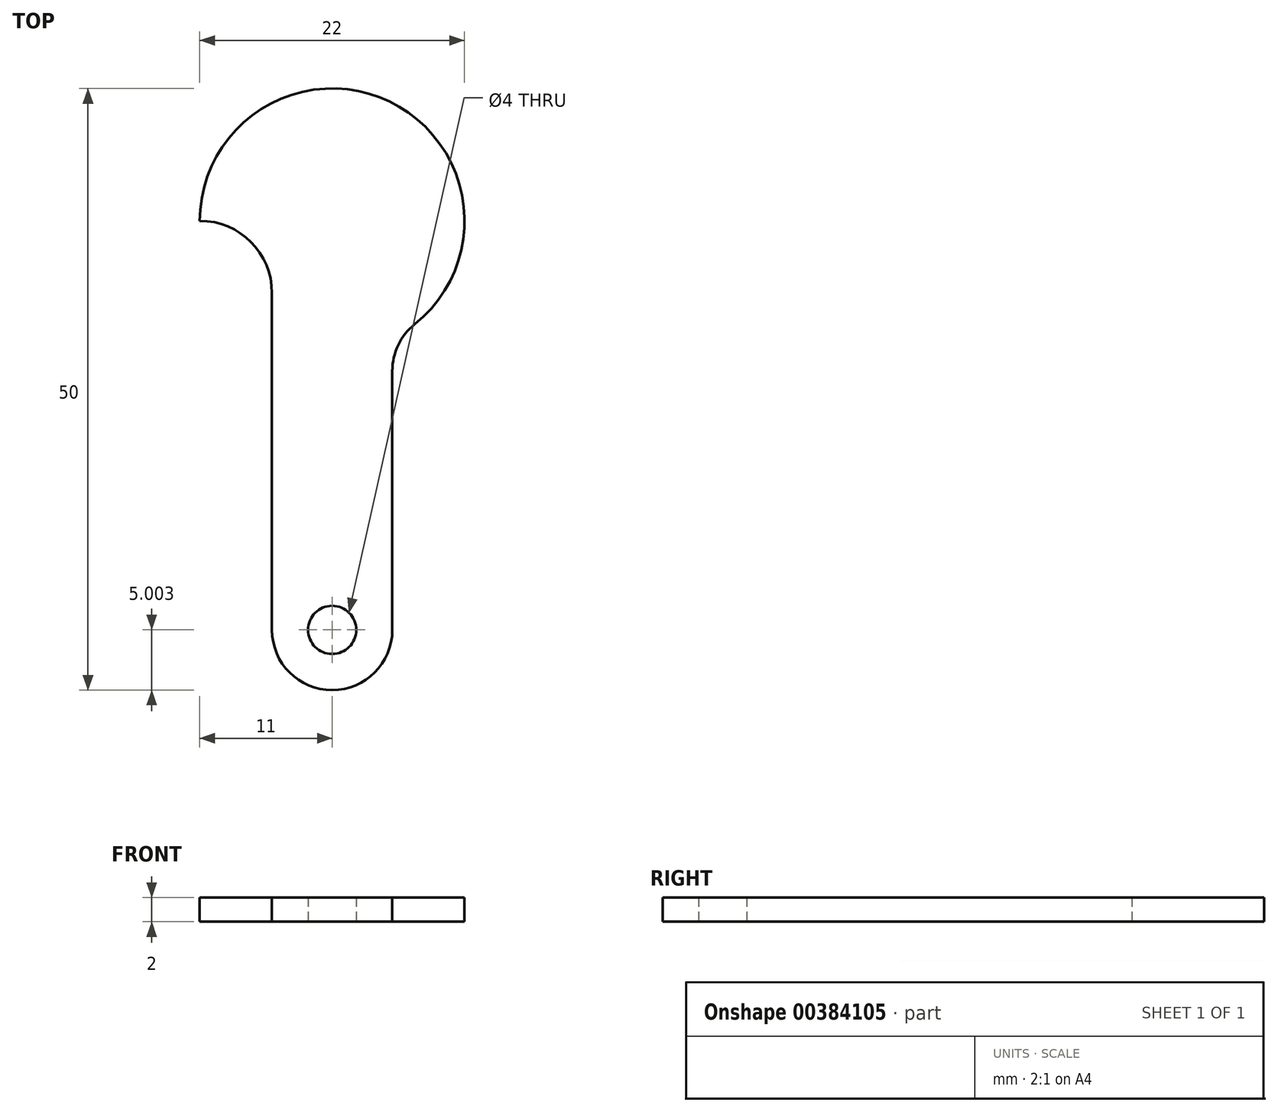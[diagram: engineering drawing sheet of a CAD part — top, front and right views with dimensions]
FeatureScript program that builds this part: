
annotation { "Feature Type Name" : "Feature", "Feature Type Description" : "" }
export const myFeature = defineFeature(function(context is Context, id is Id, definition is map)
    precondition{}
    {
        {
            var Q0;
            Q0=qCreatedBy(makeId("Top.planeOp"),FACE);
            var sketch = newSketch(context, id + "F0", { "sketchPlane" : qUnion([Q0])});
            skLineSegment(sketch, "E0", {"start": v(0, 23.22) * mm, "end": v(0, -10.78) * mm, "construction": true});
            skArc(sketch, "E1", {"start": v(-5, -10.78) * mm, "mid": v(0, -15.78) * mm, "end": v(5, -10.78) * mm});
            skLineSegment(sketch, "E2", {"start": v(0, -10.78) * mm, "end": v(5, -10.78) * mm, "construction": true});
            skLineSegment(sketch, "E3", {"start": v(0, -10.78) * mm, "end": v(-5, -10.78) * mm, "construction": true});
            skLineSegment(sketch, "E4", {"start": v(5, -10.78) * mm, "end": v(5, 10.73) * mm});
            skLineSegment(sketch, "E5", {"start": v(-5, -10.78) * mm, "end": v(-5, 17.22) * mm});
            skLineSegment(sketch, "E6", {"start": v(0, 23.22) * mm, "end": v(-11, 23.22) * mm, "construction": true});
            skArc(sketch, "E7", {"start": v(-5, 17.22) * mm, "mid": v(-6.76, 21.47) * mm, "end": v(-11, 23.22) * mm});
            skLineSegment(sketch, "E8", {"start": v(-11, 17.22) * mm, "end": v(-11, 23.22) * mm, "construction": true});
            skArc(sketch, "E9.trimOffspring", {"start": v(6.88, 14.64) * mm, "mid": v(4.76, 33.14) * mm, "end": v(-11, 23.22) * mm});
            skPoint(sketch, "E10.visualSharp", {"position": v(5, 13.43) * mm});
            skArc(sketch, "E10.filletArc", {"start": v(6.87, 14.64) * mm, "mid": v(5.5, 12.9) * mm, "end": v(5, 10.73) * mm});
            skCircle(sketch, "E11", {"center": v(0, -10.78) * mm, "radius": 2 * mm});
            skSolve(sketch);
        }
        {
            var Q0;
            Q0=makeQuery(id+"F0.imprint","IMPRINT",FACE,{"disambiguationData":[TD([[makeQuery(id+"F0.imprint","IMPRINT",EDGE,{"derivedFrom":sQuery(id+"F0.wireOp",EDGE,"E1")}),1.0]])]});
            extrude(context, id + "F1", {"entities" : qUnion([Q0]), "depth" : 2 * mm, "offsetDistance" : 25 * mm});
        }
    });
